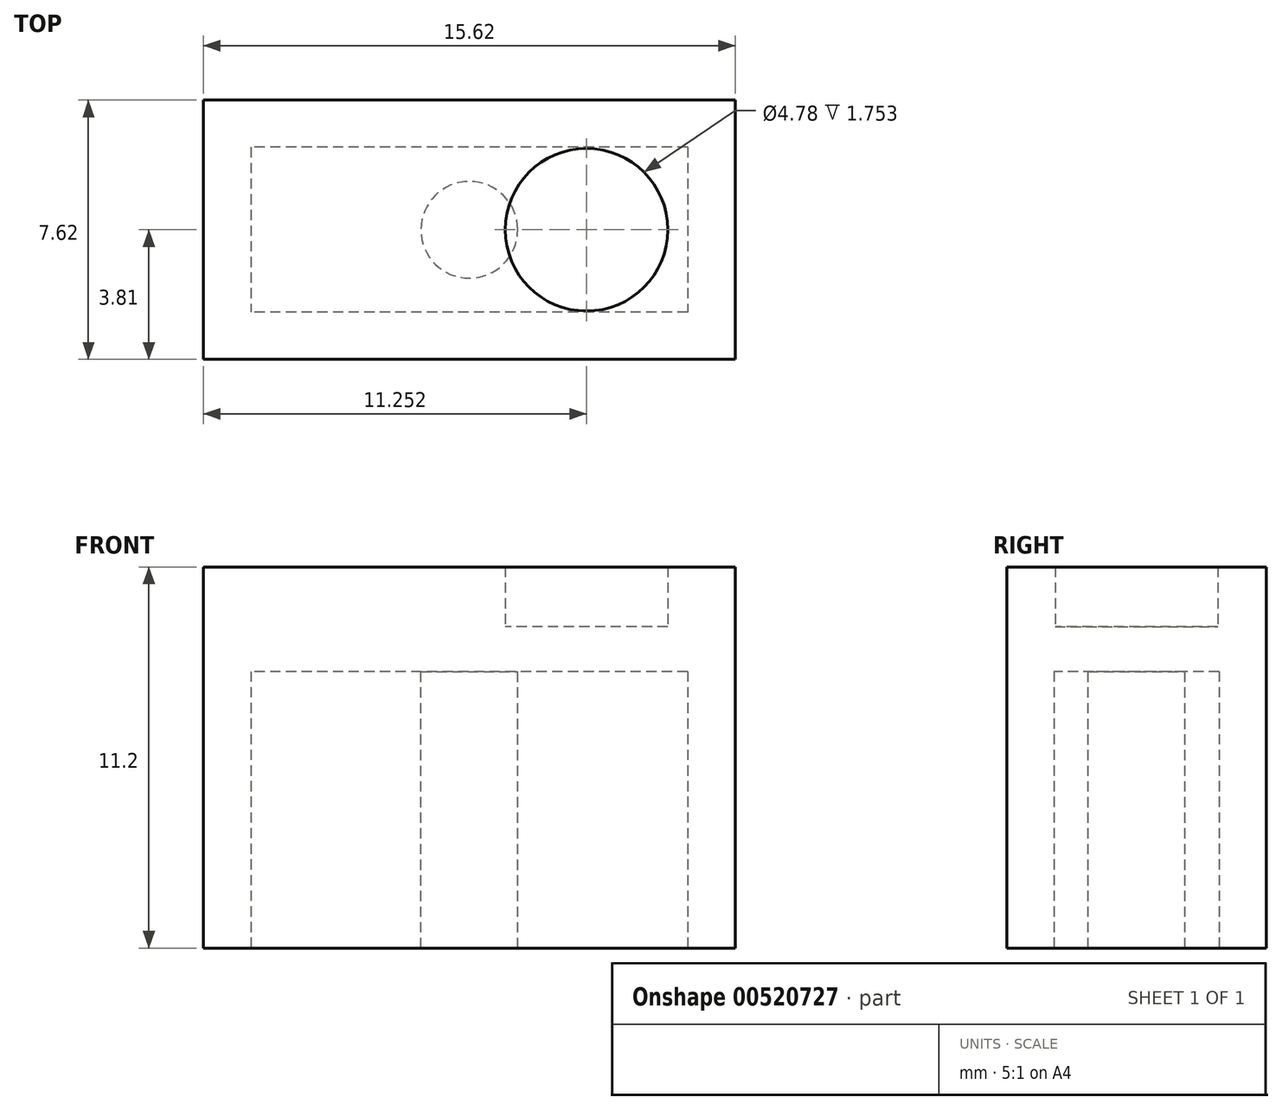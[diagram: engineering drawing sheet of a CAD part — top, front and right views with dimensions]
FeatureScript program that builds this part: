
annotation { "Feature Type Name" : "Feature", "Feature Type Description" : "" }
export const myFeature = defineFeature(function(context is Context, id is Id, definition is map)
    precondition{}
    {
        {
            var Q0;
            Q0=qCreatedBy(makeId("Top.planeOp"),FACE);
            var sketch = newSketch(context, id + "F0", { "sketchPlane" : qUnion([Q0])});
            skLineSegment(sketch, "E0.bottom", {"start": v(-7.81, 3.8) * mm, "end": v(7.81, 3.8) * mm});
            skLineSegment(sketch, "E0.top", {"start": v(-7.81, -3.8) * mm, "end": v(7.81, -3.8) * mm});
            skLineSegment(sketch, "E0.left", {"start": v(-7.81, 3.8) * mm, "end": v(-7.81, -3.8) * mm});
            skLineSegment(sketch, "E0.right", {"start": v(7.81, 3.8) * mm, "end": v(7.81, -3.8) * mm});
            skPoint(sketch, "E0.middle", {"position": v(0, 0) * mm});
            skSolve(sketch);
        }
        {
            var Q0;
            Q0=makeQuery(id+"F0.imprint","IMPRINT",FACE,{"disambiguationData":[TD([[makeQuery(id+"F0.imprint","IMPRINT",EDGE,{"derivedFrom":sQuery(id+"F0.wireOp",EDGE,"E0.bottom")}),-1.0]])]});
            extrude(context, id + "F1", {"entities" : qUnion([Q0]), "depth" : 9.45 * mm, "offsetDistance" : 25.4 * mm});
        }
        {
            var Q0;
            Q0=makeQuery(id+"F1.opExtrude","CAP_FACE",FACE,{"disambiguationData":[OSD([sQuery(id+"F0.wireOp",EDGE,"E0.bottom"),sQuery(id+"F0.wireOp",EDGE,"E0.top"),sQuery(id+"F0.wireOp",EDGE,"E0.left"),sQuery(id+"F0.wireOp",EDGE,"E0.right")])],"isStart":false});
            var sketch = newSketch(context, id + "F2", { "sketchPlane" : qUnion([Q0])});
            skCircle(sketch, "E1", {"center": v(-3.44, 0) * mm, "radius": 2.39 * mm});
            skCircle(sketch, "E2.MirrorC", {"center": v(3.44, 0) * mm, "radius": 2.39 * mm});
            skSolve(sketch);
        }
        {
            var Q0;
            Q0=makeQuery(id+"F2.imprint","IMPRINT",FACE,{"disambiguationData":[TD([[makeQuery(id+"F2.imprint","IMPRINT",EDGE,{"derivedFrom":sQuery(id+"F2.wireOp",EDGE,"E1")}),1.0]])]});
            var Q1;
            Q1=makeQuery(id+"F2.imprint","IMPRINT",FACE,{"disambiguationData":[TD([[makeQuery(id+"F2.imprint","IMPRINT",EDGE,{"derivedFrom":sQuery(id+"F2.wireOp",EDGE,"E2.MirrorC")}),-1.0]])]});
            extrude(context, id + "F3", {"entities" : qUnion([Q0, Q1]), "operationType" : NewBodyOperationType.ADD, "depth" : 1.75 * mm, "offsetDistance" : 25.4 * mm});
        }
        {
            var Q0;
            Q0=makeQuery(id+"F1.opExtrude","CAP_FACE",FACE,{"disambiguationData":[OSD([sQuery(id+"F0.wireOp",EDGE,"E0.bottom"),sQuery(id+"F0.wireOp",EDGE,"E0.top"),sQuery(id+"F0.wireOp",EDGE,"E0.left"),sQuery(id+"F0.wireOp",EDGE,"E0.right")])],"isStart":true});
            var sketch = newSketch(context, id + "F4", { "sketchPlane" : qUnion([Q0])});
            skLineSegment(sketch, "E3.bottom", {"start": v(6.41, -2.43) * mm, "end": v(-6.41, -2.43) * mm});
            skLineSegment(sketch, "E3.top", {"start": v(6.41, 2.43) * mm, "end": v(-6.41, 2.43) * mm});
            skLineSegment(sketch, "E3.left", {"start": v(6.41, -2.43) * mm, "end": v(6.41, 2.43) * mm});
            skLineSegment(sketch, "E3.right", {"start": v(-6.41, -2.43) * mm, "end": v(-6.41, 2.43) * mm});
            skPoint(sketch, "E3.middle", {"position": v(0, 0) * mm});
            skSolve(sketch);
        }
        {
            var Q0;
            Q0=makeQuery(id+"F4.imprint","IMPRINT",FACE,{"disambiguationData":[TD([[makeQuery(id+"F4.imprint","IMPRINT",EDGE,{"derivedFrom":sQuery(id+"F4.wireOp",EDGE,"E3.bottom")}),-1.0]])]});
            extrude(context, id + "F5", {"entities" : qUnion([Q0]), "operationType" : NewBodyOperationType.REMOVE, "oppositeDirection" : true, "depth" : 8.13 * mm, "offsetDistance" : 25.4 * mm});
        }
        {
            var Q0;
            Q0=makeQuery(id+"F5.boolean.opBoolean","COPY",FACE,{"derivedFrom":makeQuery(id+"F5.opExtrude","CAP_FACE",FACE,{"disambiguationData":[OSD([sQuery(id+"F4.wireOp",EDGE,"E3.bottom"),sQuery(id+"F4.wireOp",EDGE,"E3.top"),sQuery(id+"F4.wireOp",EDGE,"E3.left"),sQuery(id+"F4.wireOp",EDGE,"E3.right")])],"isStart":false})});
            var sketch = newSketch(context, id + "F6", { "sketchPlane" : qUnion([Q0])});
            skCircle(sketch, "E4", {"center": v(0, 0) * mm, "radius": 1.42 * mm});
            skSolve(sketch);
        }
        {
            var Q0;
            Q0=makeQuery(id+"F6.imprint","IMPRINT",FACE,{"disambiguationData":[TD([[makeQuery(id+"F6.imprint","IMPRINT",EDGE,{"derivedFrom":sQuery(id+"F6.wireOp",EDGE,"E4")}),1.0]])]});
            extrude(context, id + "F7", {"entities" : qUnion([Q0]), "operationType" : NewBodyOperationType.ADD, "depth" : 8.13 * mm, "offsetDistance" : 25.4 * mm});
        }
    });
